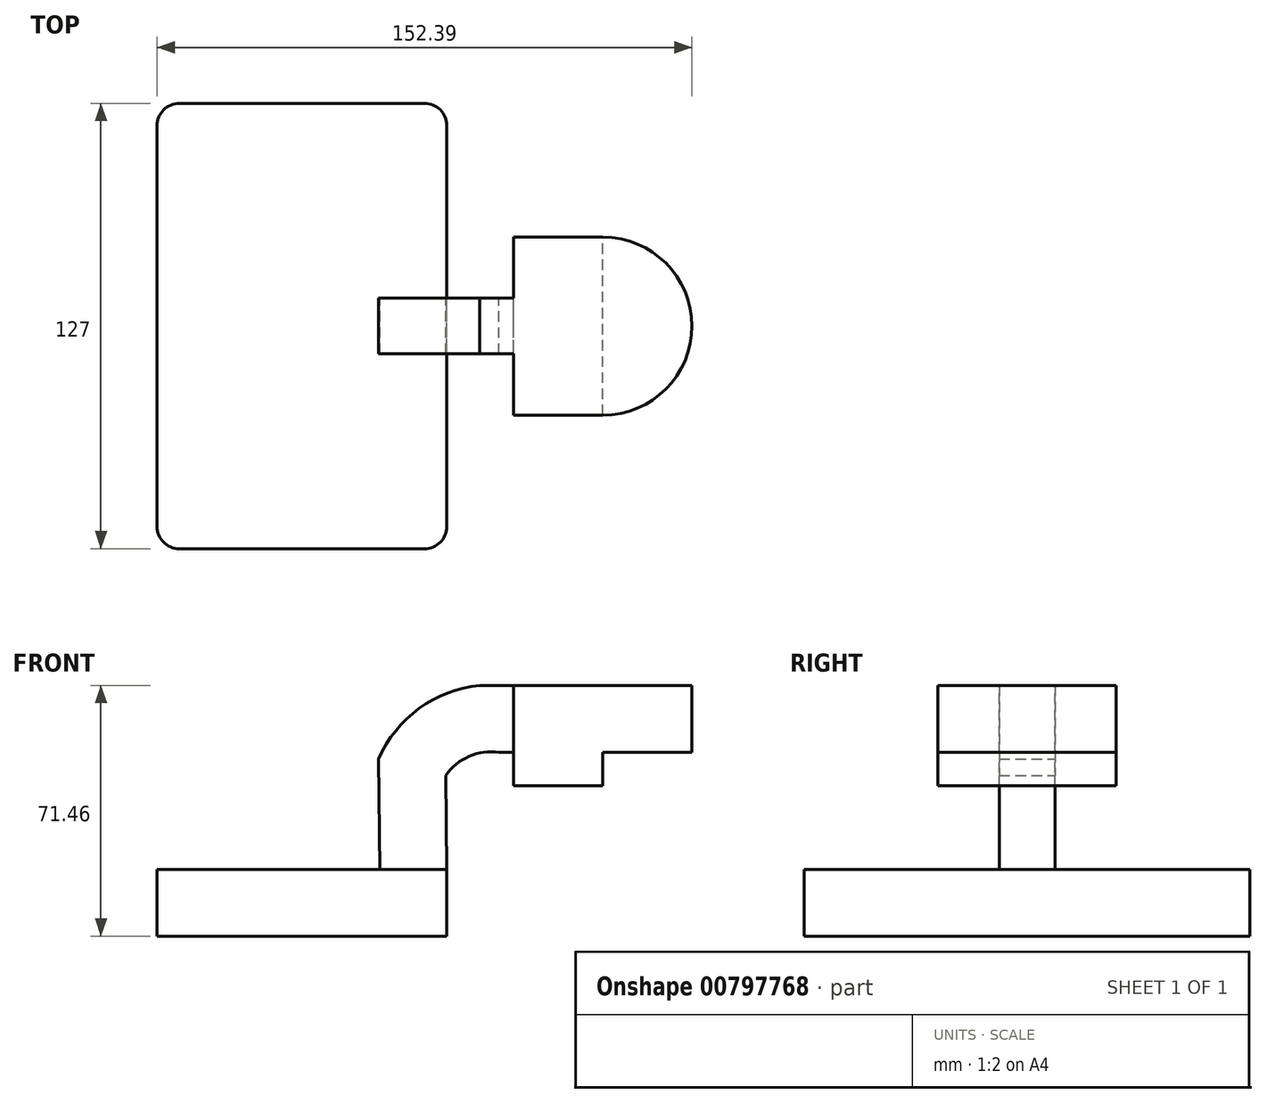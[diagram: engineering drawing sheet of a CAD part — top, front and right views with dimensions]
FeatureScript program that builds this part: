
annotation { "Feature Type Name" : "Feature", "Feature Type Description" : "" }
export const myFeature = defineFeature(function(context is Context, id is Id, definition is map)
    precondition{}
    {
        {
            var Q0;
            Q0=qCreatedBy(makeId("Front.planeOp"),FACE);
            var sketch = newSketch(context, id + "F0", { "sketchPlane" : qUnion([Q0])});
            skLineSegment(sketch, "E0.bottom", {"start": v(41.28, -9.52) * mm, "end": v(-41.27, -9.53) * mm});
            skLineSegment(sketch, "E0.top", {"start": v(41.27, 9.53) * mm, "end": v(-41.28, 9.53) * mm});
            skLineSegment(sketch, "E0.left", {"start": v(41.28, -9.52) * mm, "end": v(41.28, 9.53) * mm});
            skLineSegment(sketch, "E0.right", {"start": v(-41.27, -9.52) * mm, "end": v(-41.28, 9.53) * mm});
            skPoint(sketch, "E0.middle", {"position": v(0, 0) * mm});
            skLineSegment(sketch, "E1.bottom", {"start": v(60.32, 33.35) * mm, "end": v(111.12, 33.35) * mm});
            skLineSegment(sketch, "E1.top", {"start": v(60.32, 61.93) * mm, "end": v(111.12, 61.93) * mm});
            skLineSegment(sketch, "E1.left", {"start": v(60.32, 33.35) * mm, "end": v(60.32, 61.93) * mm});
            skLineSegment(sketch, "E1.right", {"start": v(111.12, 33.35) * mm, "end": v(111.12, 61.93) * mm});
            skPoint(sketch, "E1.middle", {"position": v(85.72, 47.64) * mm});
            skArc(sketch, "E2", {"start": v(40.97, 36.3) * mm, "mid": v(47.63, 41.72) * mm, "end": v(56.15, 42.88) * mm});
            skLineSegment(sketch, "E3", {"start": v(56.15, 42.88) * mm, "end": v(85.72, 42.88) * mm});
            skLineSegment(sketch, "E4", {"start": v(41.28, 9.53) * mm, "end": v(40.97, 36.3) * mm});
            skLineSegment(sketch, "E5.0", {"start": v(50.66, 61.93) * mm, "end": v(85.72, 61.93) * mm});
            skArc(sketch, "E5.1", {"start": v(21.86, 40.96) * mm, "mid": v(33.39, 55.39) * mm, "end": v(50.66, 61.93) * mm});
            skLineSegment(sketch, "E5.2", {"start": v(22.23, 9.3) * mm, "end": v(21.86, 40.96) * mm});
            skFitSpline(sketch, "E6", {"points": [v(-41.28, 9.52) * mm, v(50.66, 61.93) * mm], "startDerivative": vector(-46.34, 145.17) * mm, "endDerivative": vector(111.1, -13.43) * mm});
            skLineSegment(sketch, "E7", {"start": v(85.73, 61.93) * mm, "end": v(85.73, 42.88) * mm});
            skPoint(sketch, "E8", {"position": v(85.72, 33.35) * mm});
            skLineSegment(sketch, "E9", {"start": v(85.72, 42.88) * mm, "end": v(85.72, 33.35) * mm});
            skSolve(sketch);
        }
        {
            var Q0;
            Q0=makeQuery(id+"F0.imprint","IMPRINT",FACE,{"disambiguationData":[TD([[makeQuery(id+"F0.imprint","IMPRINT",EDGE,{"derivedFrom":sQuery(id+"F0.wireOp",EDGE,"E0.bottom")}),-1.0]])]});
            extrude(context, id + "F1", {"entities" : qUnion([Q0]), "endBound" : BoundingType.SYMMETRIC, "depth" : 127 * mm, "offsetDistance" : 25.4 * mm});
        }
        {
            var Q0;
            {var subQ1=sQuery(id+"F0.wireOp",EDGE,"E2");Q0=makeQuery(id+"F0.imprint","IMPRINT",FACE,{"disambiguationData":[TD([[makeQuery(id+"F0.imprint","IMPRINT",EDGE,{"derivedFrom":subQ1}),1.0]])]});}
            var Q1;
            {var subQ5=sQuery(id+"F0.wireOp",EDGE,"E7");Q1=makeQuery(id+"F0.imprint","IMPRINT",FACE,{"disambiguationData":[TD([[makeQuery(id+"F0.imprint","IMPRINT",EDGE,{"derivedFrom":subQ5}),-1.0]])]});}
            var Q2;
            {var subQ3=sQuery(id+"F0.wireOp",EDGE,"E9");Q2=makeQuery(id+"F0.imprint","IMPRINT",FACE,{"disambiguationData":[TD([[makeQuery(id+"F0.imprint","IMPRINT",EDGE,{"derivedFrom":subQ3}),-1.0]])]});}
            extrude(context, id + "F2", {"entities" : qUnion([Q0, Q1, Q2]), "operationType" : NewBodyOperationType.ADD, "endBound" : BoundingType.SYMMETRIC, "depth" : 50.8 * mm, "offsetDistance" : 25.4 * mm});
        }
        {
            var Q0;
            {var subQ4=sQuery(id+"F0.wireOp",EDGE,"E5.1");Q0=makeQuery(id+"F0.imprint","IMPRINT",FACE,{"disambiguationData":[TD([[makeQuery(id+"F0.imprint","IMPRINT",EDGE,{"derivedFrom":subQ4}),1.0]])]});}
            extrude(context, id + "F3", {"entities" : qUnion([Q0]), "operationType" : NewBodyOperationType.ADD, "endBound" : BoundingType.SYMMETRIC, "depth" : 15.88 * mm, "offsetDistance" : 25.4 * mm});
        }
        {
            var Q0;
            Q0=makeQuery(id+"F0.imprint","IMPRINT",FACE,{"disambiguationData":[TD([[makeQuery(id+"F0.imprint","IMPRINT",EDGE,{"derivedFrom":sQuery(id+"F0.wireOp",EDGE,"E1.top")}),-1.0]])]});
            var Q1;
            Q1=sQuery(id+"F0.wireOp",EDGE,"E7");
            revolve(context, id + "F4", {"operationType" : NewBodyOperationType.ADD, "surfaceOperationType" : NewSurfaceOperationType.NEW, "entities" : qUnion([Q0]), "axis" : qUnion([Q1]), "revolveType" : RevolveType.FULL});
        }
        {
            var Q0;
            Q0=makeQuery(id+"F1.opExtrude","CAP_EDGE",EDGE,{"disambiguationData":[OSD([sQuery(id+"F0.wireOp",EDGE,"E0.left")])],"isStart":true});
            var Q1;
            Q1=makeQuery(id+"F1.opExtrude","CAP_EDGE",EDGE,{"disambiguationData":[OSD([sQuery(id+"F0.wireOp",EDGE,"E0.right")])],"isStart":true});
            var Q2;
            Q2=makeQuery(id+"F1.opExtrude","CAP_EDGE",EDGE,{"disambiguationData":[OSD([sQuery(id+"F0.wireOp",EDGE,"E0.right")])],"isStart":false});
            var Q3;
            Q3=makeQuery(id+"F1.opExtrude","CAP_EDGE",EDGE,{"disambiguationData":[OSD([sQuery(id+"F0.wireOp",EDGE,"E0.left")])],"isStart":false});
            fillet(context, id + "F5", {"entities" : qUnion([Q0, Q1, Q2, Q3]), "radius" : 6.35 * mm, "tangentPropagation" : true, "allowEdgeOverflow" : false});
        }
    });
